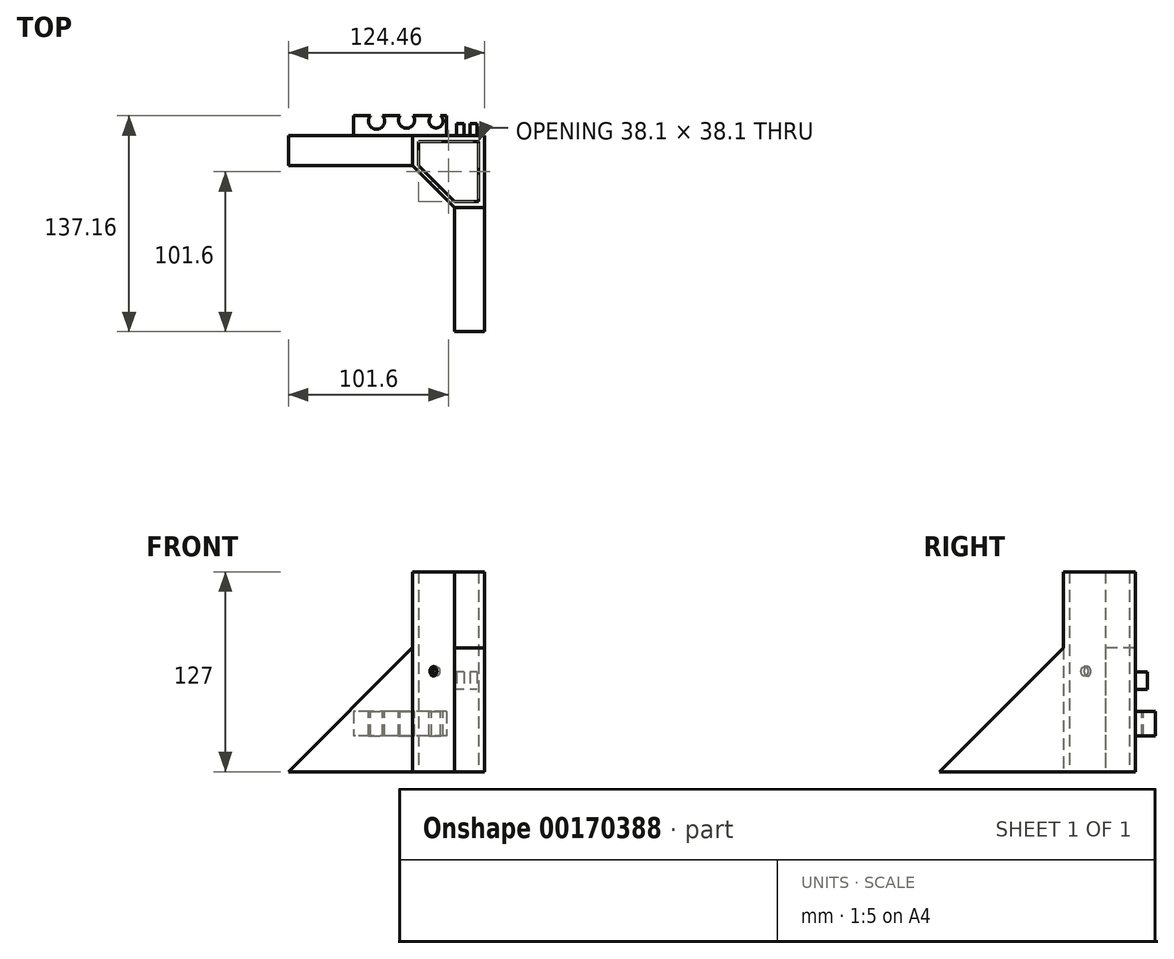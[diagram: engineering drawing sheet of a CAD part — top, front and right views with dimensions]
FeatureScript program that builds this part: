
annotation { "Feature Type Name" : "Feature", "Feature Type Description" : "" }
export const myFeature = defineFeature(function(context is Context, id is Id, definition is map)
    precondition{}
    {
        {
            var Q0;
            Q0=qCreatedBy(makeId("Top.planeOp"),FACE);
            var sketch = newSketch(context, id + "F0", { "sketchPlane" : qUnion([Q0])});
            skLineSegment(sketch, "E0.bottom", {"start": v(-19.05, 19.05) * mm, "end": v(19.05, 19.05) * mm});
            skLineSegment(sketch, "E0.top", {"start": v(-19.05, -19.05) * mm, "end": v(19.05, -19.05) * mm});
            skLineSegment(sketch, "E0.left", {"start": v(-19.05, 19.05) * mm, "end": v(-19.05, -19.05) * mm});
            skLineSegment(sketch, "E0.right", {"start": v(19.05, 19.05) * mm, "end": v(19.05, -19.05) * mm});
            skPoint(sketch, "E0.middle", {"position": v(0, 0) * mm});
            skLineSegment(sketch, "E1", {"start": v(-19.05, 19.05) * mm, "end": v(-19.05, 3.8) * mm});
            skLineSegment(sketch, "E2", {"start": v(19.05, -19.05) * mm, "end": v(3.81, -19.05) * mm});
            skLineSegment(sketch, "E3", {"start": v(-19.05, 3.8) * mm, "end": v(3.8, -19.05) * mm});
            skLineSegment(sketch, "E4", {"start": v(-22.65, 3.8) * mm, "end": v(-22.65, 22.86) * mm});
            skLineSegment(sketch, "E5", {"start": v(-22.65, 22.86) * mm, "end": v(22.86, 22.86) * mm});
            skLineSegment(sketch, "E6", {"start": v(22.86, 22.86) * mm, "end": v(22.86, -22.86) * mm});
            skLineSegment(sketch, "E7", {"start": v(22.86, -22.86) * mm, "end": v(3.81, -22.86) * mm});
            skLineSegment(sketch, "E8", {"start": v(3.81, -22.86) * mm, "end": v(-22.65, 3.8) * mm});
            skSolve(sketch);
        }
        {
            var Q0;
            Q0=makeQuery(id+"F0.imprint","IMPRINT",FACE,{"disambiguationData":[TD([[makeQuery(id+"F0.imprint","IMPRINT",EDGE,{"derivedFrom":sQuery(id+"F0.wireOp",EDGE,"E0.bottom")}),1.0]])]});
            var Q1;
            {var subQ0=sQuery(id+"F0.wireOp",EDGE,"E3");Q1=makeQuery(id+"F0.imprint","IMPRINT",FACE,{"disambiguationData":[TD([[makeQuery(id+"F0.imprint","IMPRINT",EDGE,{"derivedFrom":subQ0}),-1.0]])]});}
            extrude(context, id + "F1", {"entities" : qUnion([Q0, Q1]), "depth" : 127 * mm});
        }
        {
            var Q0;
            Q0=makeQuery(id+"F1.opExtrude","SWEPT_FACE",FACE,{"disambiguationData":[OSD([sQuery(id+"F0.wireOp",EDGE,"E6")])]});
            var sketch = newSketch(context, id + "F2", { "sketchPlane" : qUnion([Q0])});
            skLineSegment(sketch, "E9", {"start": v(0, 101.6) * mm, "end": v(-101.6, 0) * mm});
            skLineSegment(sketch, "E10", {"start": v(-101.6, 0) * mm, "end": v(0, 0) * mm});
            skLineSegment(sketch, "E11", {"start": v(0, 0) * mm, "end": v(0, 101.6) * mm});
            skSolve(sketch);
        }
        {
            var Q0;
            {var subQ0=sQuery(id+"F2.wireOp",EDGE,"E10");var subQ1=sQuery(id+"F2.wireOp",EDGE,"E9");var subQ2=makeQuery(id+"F2.imprint","INTERSECT",VERTEX,{"derivedFrom":[subQ1,subQ0]});Q0=makeQuery(id+"F2.imprint","IMPRINT",FACE,{"disambiguationData":[TD([[makeQuery(id+"F2.imprint","IMPRINT",EDGE,{"disambiguationData":[TD([[subQ2,1.0]])],"derivedFrom":subQ1}),1.0]])]});}
            extrude(context, id + "F3", {"entities" : qUnion([Q0]), "operationType" : NewBodyOperationType.ADD, "oppositeDirection" : true, "depth" : 19.05 * mm});
        }
        {
            var Q0;
            Q0=makeQuery(id+"F1.opExtrude","SWEPT_FACE",FACE,{"disambiguationData":[OSD([sQuery(id+"F0.wireOp",EDGE,"E5")])]});
            var sketch = newSketch(context, id + "F4", { "sketchPlane" : qUnion([Q0])});
            skLineSegment(sketch, "E12", {"start": v(0, 101.6) * mm, "end": v(101.6, 0) * mm});
            skLineSegment(sketch, "E13", {"start": v(101.6, 0) * mm, "end": v(0, 0) * mm});
            skLineSegment(sketch, "E14", {"start": v(0, 0) * mm, "end": v(0, 101.6) * mm});
            skSolve(sketch);
        }
        {
            var Q0;
            {var subQ0=sQuery(id+"F4.wireOp",EDGE,"E13");var subQ1=sQuery(id+"F4.wireOp",EDGE,"E12");var subQ2=makeQuery(id+"F4.imprint","INTERSECT",VERTEX,{"derivedFrom":[subQ1,subQ0]});Q0=makeQuery(id+"F4.imprint","IMPRINT",FACE,{"disambiguationData":[TD([[makeQuery(id+"F4.imprint","IMPRINT",EDGE,{"disambiguationData":[TD([[subQ2,1.0]])],"derivedFrom":subQ1}),-1.0]])]});}
            extrude(context, id + "F5", {"entities" : qUnion([Q0]), "operationType" : NewBodyOperationType.ADD, "oppositeDirection" : true, "depth" : 19.05 * mm});
        }
        {
            var Q0;
            Q0=makeQuery(id+"F1.opExtrude","SWEPT_FACE",FACE,{"disambiguationData":[OSD([sQuery(id+"F0.wireOp",EDGE,"E8")])]});
            var sketch = newSketch(context, id + "F6", { "sketchPlane" : qUnion([Q0])});
            skCircle(sketch, "E15", {"center": v(0, 63.76) * mm, "radius": 3.04 * mm});
            skSolve(sketch);
        }
        {
            var Q0;
            Q0=makeQuery(id+"F6.imprint","IMPRINT",FACE,{"disambiguationData":[TD([[makeQuery(id+"F6.imprint","IMPRINT",EDGE,{"derivedFrom":sQuery(id+"F6.wireOp",EDGE,"E15")}),1.0]])]});
            extrude(context, id + "F7", {"entities" : qUnion([Q0]), "operationType" : NewBodyOperationType.REMOVE, "oppositeDirection" : true, "depth" : 25.4 * mm});
        }
        {
            var Q0;
            {var subQ0=sQuery(id+"F0.wireOp",EDGE,"E5");Q0=makeQuery(id+"F5.boolean.opBoolean","MERGE",FACE,{"derivedFrom":[makeQuery(id+"F1.opExtrude","SWEPT_FACE",FACE,{"disambiguationData":[OSD([subQ0])]}),makeQuery(id+"F5.opExtrude","CAP_FACE",FACE,{"disambiguationData":[OSD([sQuery(id+"F0.wireOp",EDGE,"E4"),subQ0,sQuery(id+"F4.wireOp",EDGE,"E12"),sQuery(id+"F4.wireOp",EDGE,"E13")])],"isStart":true})]});}
            var sketch = newSketch(context, id + "F8", { "sketchPlane" : qUnion([Q0])});
            skLineSegment(sketch, "E16", {"start": v(-22.86, 101.22) * mm, "end": v(22.65, 101.22) * mm});
            skLineSegment(sketch, "E17", {"start": v(-22.86, 88.28) * mm, "end": v(22.65, 88.28) * mm});
            skLineSegment(sketch, "E18.bottom", {"start": v(-18.26, 101.22) * mm, "end": v(-13.86, 101.22) * mm});
            skLineSegment(sketch, "E18.top", {"start": v(-18.26, 88.28) * mm, "end": v(-13.86, 88.28) * mm});
            skLineSegment(sketch, "E18.left", {"start": v(-18.26, 101.22) * mm, "end": v(-18.26, 88.28) * mm});
            skLineSegment(sketch, "E18.right", {"start": v(-13.86, 101.22) * mm, "end": v(-13.86, 88.28) * mm});
            skLineSegment(sketch, "E19.bottom", {"start": v(-9.8, 101.22) * mm, "end": v(-5.2, 101.22) * mm});
            skLineSegment(sketch, "E19.top", {"start": v(-9.8, 88.28) * mm, "end": v(-5.2, 88.28) * mm});
            skLineSegment(sketch, "E19.left", {"start": v(-9.8, 101.22) * mm, "end": v(-9.8, 88.28) * mm});
            skLineSegment(sketch, "E19.right", {"start": v(-5.2, 101.22) * mm, "end": v(-5.2, 88.28) * mm});
            skLineSegment(sketch, "E20", {"start": v(-22.86, 63.5) * mm, "end": v(35.48, 63.5) * mm});
            skLineSegment(sketch, "E21", {"start": v(-22.86, 52.23) * mm, "end": v(38.52, 52.23) * mm});
            skLineSegment(sketch, "E22", {"start": v(-18.26, 88.28) * mm, "end": v(-18.26, 52.23) * mm});
            skLineSegment(sketch, "E23", {"start": v(-13.86, 88.28) * mm, "end": v(-13.86, 52.23) * mm});
            skLineSegment(sketch, "E24", {"start": v(-9.8, 88.28) * mm, "end": v(-9.8, 52.23) * mm});
            skLineSegment(sketch, "E25", {"start": v(-5.2, 88.28) * mm, "end": v(-5.2, 52.23) * mm});
            skLineSegment(sketch, "E26.bottom", {"start": v(1.32, 38.35) * mm, "end": v(60.31, 38.35) * mm});
            skLineSegment(sketch, "E26.top", {"start": v(1.32, 22.71) * mm, "end": v(60.31, 22.71) * mm});
            skLineSegment(sketch, "E26.left", {"start": v(1.32, 38.35) * mm, "end": v(1.32, 22.71) * mm});
            skLineSegment(sketch, "E26.right", {"start": v(60.31, 38.35) * mm, "end": v(60.31, 22.71) * mm});
            skPoint(sketch, "E26.middle", {"position": v(30.82, 30.53) * mm});
            skSolve(sketch);
        }
        {
            var Q0;
            Q0=makeQuery(id+"F8.imprint","IMPRINT",FACE,{"disambiguationData":[TD([[makeQuery(id+"F8.imprint","IMPRINT",EDGE,{"derivedFrom":sQuery(id+"F8.wireOp",EDGE,"E18.bottom")}),-1.0]])]});
            var Q1;
            Q1=makeQuery(id+"F8.imprint","IMPRINT",FACE,{"disambiguationData":[TD([[makeQuery(id+"F8.imprint","IMPRINT",EDGE,{"derivedFrom":sQuery(id+"F8.wireOp",EDGE,"E19.bottom")}),-1.0]])]});
            var Q2;
            {var subQ0=sQuery(id+"F8.wireOp",EDGE,"E22");var subQ1=sQuery(id+"F8.wireOp",EDGE,"E20");var subQ2=makeQuery(id+"F8.imprint","INTERSECT",VERTEX,{"derivedFrom":[subQ1,subQ0]});Q2=makeQuery(id+"F8.imprint","IMPRINT",FACE,{"disambiguationData":[TD([[makeQuery(id+"F8.imprint","IMPRINT",EDGE,{"disambiguationData":[TD([[subQ2,-1.0]])],"derivedFrom":subQ1}),-1.0]])]});}
            var Q3;
            {var subQ0=sQuery(id+"F8.wireOp",EDGE,"E25");var subQ1=sQuery(id+"F8.wireOp",EDGE,"E20");var subQ2=makeQuery(id+"F8.imprint","INTERSECT",VERTEX,{"derivedFrom":[subQ1,subQ0]});Q3=makeQuery(id+"F8.imprint","IMPRINT",FACE,{"disambiguationData":[TD([[makeQuery(id+"F8.imprint","IMPRINT",EDGE,{"disambiguationData":[TD([[subQ2,1.0]])],"derivedFrom":subQ1}),-1.0]])]});}
            extrude(context, id + "F9", {"entities" : qUnion([Q0, Q1, Q2, Q3]), "operationType" : NewBodyOperationType.ADD, "depth" : 7.62 * mm});
        }
        {
            var Q0;
            Q0=makeQuery(id+"F8.imprint","IMPRINT",FACE,{"disambiguationData":[TD([[makeQuery(id+"F8.imprint","IMPRINT",EDGE,{"derivedFrom":sQuery(id+"F8.wireOp",EDGE,"E26.bottom")}),-1.0]])]});
            extrude(context, id + "F10", {"entities" : qUnion([Q0]), "operationType" : NewBodyOperationType.ADD, "depth" : 12.7 * mm});
        }
        {
            var Q0;
            Q0=makeQuery(id+"F10.opExtrude","SWEPT_FACE",FACE,{"disambiguationData":[OSD([sQuery(id+"F8.wireOp",EDGE,"E26.bottom")])]});
            var sketch = newSketch(context, id + "F11", { "sketchPlane" : qUnion([Q0])});
            skArc(sketch, "E27", {"start": v(-10.85, 35.56) * mm, "mid": v(-7.85, 27.84) * mm, "end": v(-4.84, 35.56) * mm});
            skArc(sketch, "E28", {"start": v(-30.82, 35.56) * mm, "mid": v(-26.57, 27.65) * mm, "end": v(-22.32, 35.56) * mm});
            skArc(sketch, "E29", {"start": v(-49.53, 35.56) * mm, "mid": v(-45.62, 27.04) * mm, "end": v(-41.7, 35.56) * mm});
            skSolve(sketch);
        }
        {
            var Q0;
            {var subQ0=sQuery(id+"F11.wireOp",EDGE,"E29");Q0=makeQuery(id+"F11.imprint","IMPRINT",FACE,{"disambiguationData":[TD([[makeQuery(id+"F11.imprint","IMPRINT",EDGE,{"derivedFrom":subQ0}),1.0]])]});}
            var Q1;
            {var subQ0=sQuery(id+"F11.wireOp",EDGE,"E28");Q1=makeQuery(id+"F11.imprint","IMPRINT",FACE,{"disambiguationData":[TD([[makeQuery(id+"F11.imprint","IMPRINT",EDGE,{"derivedFrom":subQ0}),1.0]])]});}
            var Q2;
            {var subQ0=sQuery(id+"F11.wireOp",EDGE,"E27");Q2=makeQuery(id+"F11.imprint","IMPRINT",FACE,{"disambiguationData":[TD([[makeQuery(id+"F11.imprint","IMPRINT",EDGE,{"derivedFrom":subQ0}),1.0]])]});}
            extrude(context, id + "F12", {"entities" : qUnion([Q0, Q1, Q2]), "operationType" : NewBodyOperationType.REMOVE, "oppositeDirection" : true, "depth" : 25.4 * mm});
        }
    });
